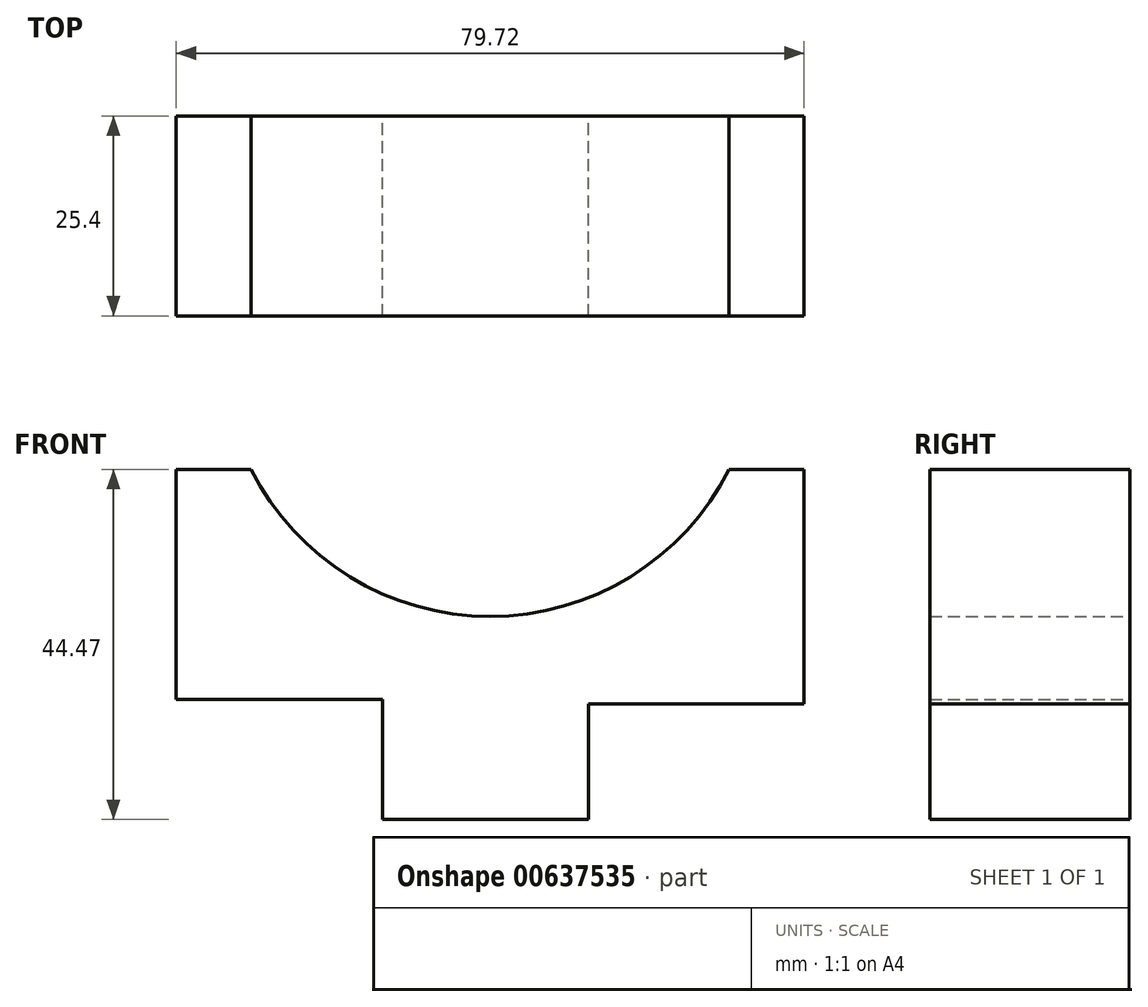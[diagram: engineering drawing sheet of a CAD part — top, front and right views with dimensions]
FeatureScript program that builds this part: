
annotation { "Feature Type Name" : "Feature", "Feature Type Description" : "" }
export const myFeature = defineFeature(function(context is Context, id is Id, definition is map)
    precondition{}
    {
        {
            var Q0;
            Q0=qCreatedBy(makeId("Front.planeOp"),FACE);
            var sketch = newSketch(context, id + "F0", { "sketchPlane" : qUnion([Q0])});
            skLineSegment(sketch, "E0", {"start": v(-12.23, -44.47) * mm, "end": v(13.96, -44.47) * mm});
            skLineSegment(sketch, "E1", {"start": v(13.96, -44.47) * mm, "end": v(13.96, -29.79) * mm});
            skLineSegment(sketch, "E2", {"start": v(13.96, -29.79) * mm, "end": v(41.3, -29.79) * mm});
            skLineSegment(sketch, "E3", {"start": v(41.3, -29.79) * mm, "end": v(41.3, 0) * mm});
            skLineSegment(sketch, "E4", {"start": v(41.3, 0) * mm, "end": v(31.8, 0) * mm});
            skLineSegment(sketch, "E5", {"start": v(-12.23, -44.47) * mm, "end": v(-12.23, -29.21) * mm});
            skLineSegment(sketch, "E6", {"start": v(-12.23, -29.21) * mm, "end": v(-38.42, -29.21) * mm});
            skLineSegment(sketch, "E7", {"start": v(-38.42, -29.21) * mm, "end": v(-38.42, 0) * mm});
            skLineSegment(sketch, "E8", {"start": v(-38.42, 0) * mm, "end": v(-28.92, 0) * mm});
            skArc(sketch, "E9", {"start": v(-28.92, 0) * mm, "mid": v(1.44, -18.68) * mm, "end": v(31.8, 0) * mm});
            skSolve(sketch);
        }
        {
            var Q0;
            Q0 = qSketchRegion(id + "F0", true);
            extrude(context, id + "F1", {"entities" : qUnion([Q0]), "depth" : 25.4 * mm, "offsetDistance" : 25.4 * mm});
        }
    });
